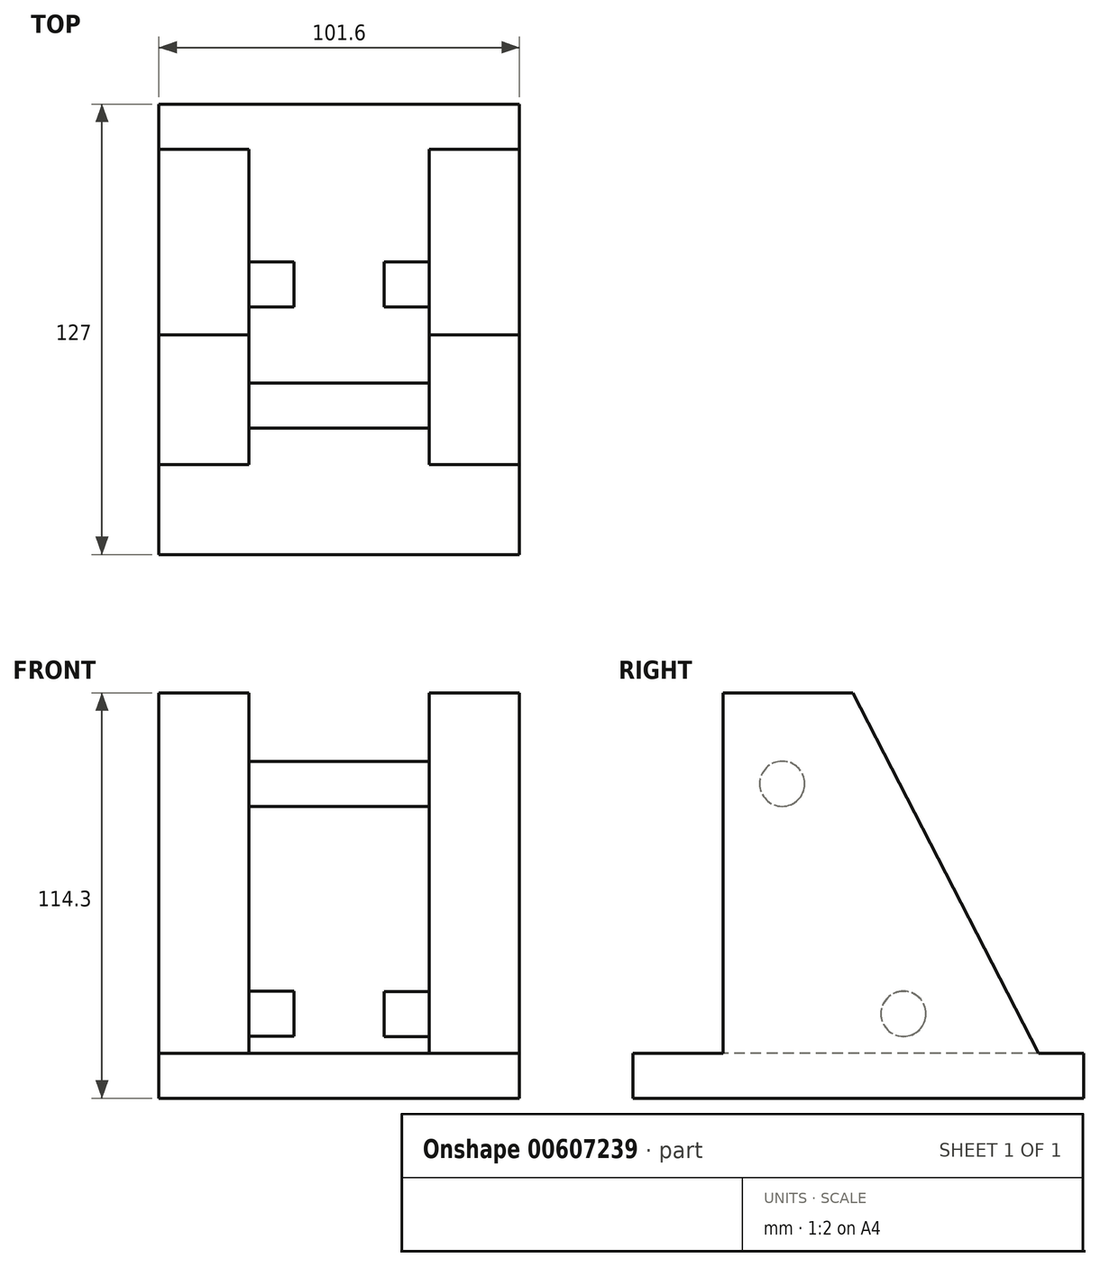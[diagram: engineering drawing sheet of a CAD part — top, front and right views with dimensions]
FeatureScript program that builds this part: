
annotation { "Feature Type Name" : "Feature", "Feature Type Description" : "" }
export const myFeature = defineFeature(function(context is Context, id is Id, definition is map)
    precondition{}
    {
        {
            var Q0;
            Q0=qCreatedBy(makeId("Right.planeOp"),FACE);
            var sketch = newSketch(context, id + "F0", { "sketchPlane" : qUnion([Q0])});
            skLineSegment(sketch, "E0", {"start": v(-25.4, 63.5) * mm, "end": v(-25.4, -38.1) * mm});
            skLineSegment(sketch, "E1", {"start": v(-25.4, -38.1) * mm, "end": v(-50.8, -38.1) * mm});
            skLineSegment(sketch, "E2", {"start": v(-50.8, -38.1) * mm, "end": v(-50.8, -50.8) * mm});
            skLineSegment(sketch, "E3", {"start": v(-50.8, -50.8) * mm, "end": v(76.2, -50.8) * mm});
            skLineSegment(sketch, "E4", {"start": v(76.2, -50.8) * mm, "end": v(76.2, -38.1) * mm});
            skLineSegment(sketch, "E5", {"start": v(76.2, -38.1) * mm, "end": v(63.5, -38.1) * mm});
            skLineSegment(sketch, "E6", {"start": v(63.5, -38.1) * mm, "end": v(11.14, 63.5) * mm});
            skLineSegment(sketch, "E7", {"start": v(-25.4, 63.5) * mm, "end": v(11.14, 63.5) * mm});
            skSolve(sketch);
        }
        {
            var Q0;
            Q0=makeQuery(id+"F0.imprint","IMPRINT",FACE,{"disambiguationData":[TD([[makeQuery(id+"F0.imprint","IMPRINT",EDGE,{"derivedFrom":sQuery(id+"F0.wireOp",EDGE,"E0")}),1.0]])]});
            extrude(context, id + "F1", {"entities" : qUnion([Q0]), "endBound" : BoundingType.SYMMETRIC, "depth" : 101.6 * mm, "offsetDistance" : 25.4 * mm});
        }
        {
            var Q0;
            Q0=makeQuery(id+"F1.opExtrude","SWEPT_FACE",FACE,{"disambiguationData":[OSD([sQuery(id+"F0.wireOp",EDGE,"E0")])]});
            var sketch = newSketch(context, id + "F2", { "sketchPlane" : qUnion([Q0])});
            skLineSegment(sketch, "E8", {"start": v(-50.8, 63.5) * mm, "end": v(-25.4, 63.5) * mm, "construction": true});
            skLineSegment(sketch, "E9", {"start": v(50.8, 63.5) * mm, "end": v(25.4, 63.5) * mm, "construction": true});
            skLineSegment(sketch, "E10.bottom", {"start": v(-25.4, 63.5) * mm, "end": v(25.4, 63.5) * mm});
            skLineSegment(sketch, "E10.top", {"start": v(-25.4, -38.1) * mm, "end": v(25.4, -38.1) * mm});
            skLineSegment(sketch, "E10.left", {"start": v(-25.4, 63.5) * mm, "end": v(-25.4, -38.1) * mm});
            skLineSegment(sketch, "E10.right", {"start": v(25.4, 63.5) * mm, "end": v(25.4, -38.1) * mm});
            skSolve(sketch);
        }
        {
            var Q0;
            Q0 = qSketchRegion(id + "F2", true);
            extrude(context, id + "F3", {"entities" : qUnion([Q0]), "operationType" : NewBodyOperationType.REMOVE, "endBound" : BoundingType.THROUGH_ALL, "oppositeDirection" : true, "depth" : 50.8 * mm, "offsetDistance" : 25.4 * mm});
        }
        {
            var Q0;
            Q0=qCreatedBy(makeId("Right.planeOp"),FACE);
            var sketch = newSketch(context, id + "F4", { "sketchPlane" : qUnion([Q0])});
            skCircle(sketch, "E11", {"center": v(-8.78, 37.85) * mm, "radius": 6.35 * mm});
            skSolve(sketch);
        }
        {
            var Q0;
            Q0 = qSketchRegion(id + "F4", true);
            extrude(context, id + "F5", {"entities" : qUnion([Q0]), "operationType" : NewBodyOperationType.ADD, "endBound" : BoundingType.SYMMETRIC, "depth" : 50.8 * mm, "offsetDistance" : 25.4 * mm});
        }
        {
            var Q0;
            Q0=makeQuery(id+"F3.boolean.opBoolean","COPY",FACE,{"derivedFrom":makeQuery(id+"F3.opExtrude","SWEPT_FACE",FACE,{"disambiguationData":[OSD([sQuery(id+"F2.wireOp",EDGE,"E10.left")])]})});
            var sketch = newSketch(context, id + "F6", { "sketchPlane" : qUnion([Q0])});
            skLineSegment(sketch, "E12", {"start": v(-25.4, -26.34) * mm, "end": v(25.39, -27) * mm, "construction": true});
            skLineSegment(sketch, "E13", {"start": v(25.39, -27) * mm, "end": v(25.39, -38.1) * mm, "construction": true});
            skCircle(sketch, "E14", {"center": v(25.39, -27) * mm, "radius": 6.35 * mm});
            skSolve(sketch);
        }
        {
            var Q0;
            Q0=makeQuery(id+"F6.imprint","IMPRINT",FACE,{"disambiguationData":[TD([[makeQuery(id+"F6.imprint","IMPRINT",EDGE,{"derivedFrom":sQuery(id+"F6.wireOp",EDGE,"E14")}),1.0]])]});
            extrude(context, id + "F7", {"entities" : qUnion([Q0]), "operationType" : NewBodyOperationType.ADD, "depth" : 12.7 * mm, "offsetDistance" : 25.4 * mm});
        }
        {
            var Q0;
            Q0=makeQuery(id+"F3.boolean.opBoolean","COPY",FACE,{"derivedFrom":makeQuery(id+"F3.opExtrude","SWEPT_FACE",FACE,{"disambiguationData":[OSD([sQuery(id+"F2.wireOp",EDGE,"E10.right")])]})});
            var sketch = newSketch(context, id + "F8", { "sketchPlane" : qUnion([Q0])});
            skLineSegment(sketch, "E15", {"start": v(25.4, -27.04) * mm, "end": v(-25.4, -27.04) * mm, "construction": true});
            skLineSegment(sketch, "E16", {"start": v(-25.4, -38.1) * mm, "end": v(-25.4, -27.04) * mm, "construction": true});
            skCircle(sketch, "E17", {"center": v(-25.4, -27.04) * mm, "radius": 6.35 * mm});
            skSolve(sketch);
        }
        {
            var Q0;
            Q0=makeQuery(id+"F8.imprint","IMPRINT",FACE,{"disambiguationData":[TD([[makeQuery(id+"F8.imprint","IMPRINT",EDGE,{"derivedFrom":sQuery(id+"F8.wireOp",EDGE,"E17")}),1.0]])]});
            extrude(context, id + "F9", {"entities" : qUnion([Q0]), "operationType" : NewBodyOperationType.ADD, "depth" : 12.7 * mm, "offsetDistance" : 25.4 * mm});
        }
    });
